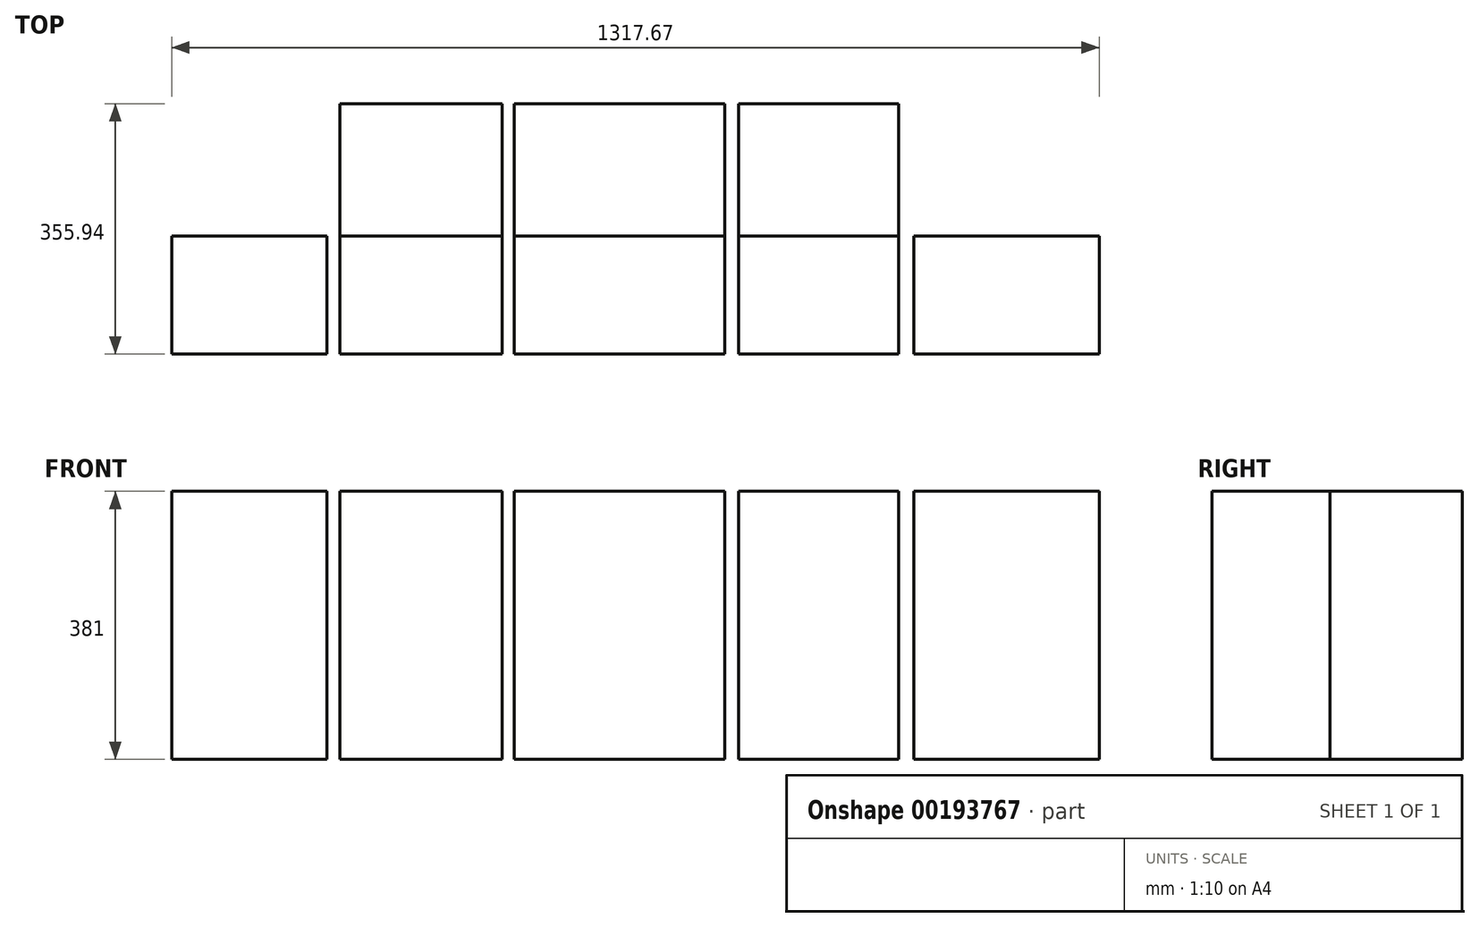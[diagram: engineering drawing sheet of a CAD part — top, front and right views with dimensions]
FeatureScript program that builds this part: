
annotation { "Feature Type Name" : "Feature", "Feature Type Description" : "" }
export const myFeature = defineFeature(function(context is Context, id is Id, definition is map)
    precondition{}
    {
        {
            var Q0;
            Q0=qCreatedBy(makeId("Top.planeOp"),FACE);
            var sketch = newSketch(context, id + "F0", { "sketchPlane" : qUnion([Q0])});
            skLineSegment(sketch, "E0.bottom", {"start": v(-149.74, -83.99) * mm, "end": v(149.74, -83.99) * mm});
            skLineSegment(sketch, "E0.top", {"start": v(-149.74, 83.99) * mm, "end": v(149.74, 83.99) * mm});
            skLineSegment(sketch, "E0.left", {"start": v(-149.74, -83.99) * mm, "end": v(-149.74, 83.99) * mm});
            skLineSegment(sketch, "E0.right", {"start": v(149.74, -83.99) * mm, "end": v(149.74, 83.99) * mm});
            skPoint(sketch, "E0.middle", {"position": v(0, 0) * mm});
            skLineSegment(sketch, "E1.bottom", {"start": v(-166.81, 83.99) * mm, "end": v(-397.4, 83.99) * mm});
            skLineSegment(sketch, "E1.top", {"start": v(-166.81, -83.99) * mm, "end": v(-397.4, -83.99) * mm});
            skLineSegment(sketch, "E1.left", {"start": v(-166.81, 83.99) * mm, "end": v(-166.81, -83.99) * mm});
            skLineSegment(sketch, "E1.right", {"start": v(-397.4, 83.99) * mm, "end": v(-397.4, -83.99) * mm});
            skLineSegment(sketch, "E2.bottom", {"start": v(-415.52, 83.99) * mm, "end": v(-636.23, 83.99) * mm});
            skLineSegment(sketch, "E2.top", {"start": v(-415.52, -83.99) * mm, "end": v(-636.23, -83.99) * mm});
            skLineSegment(sketch, "E2.left", {"start": v(-415.52, 83.99) * mm, "end": v(-415.52, -83.99) * mm});
            skLineSegment(sketch, "E2.right", {"start": v(-636.23, 83.99) * mm, "end": v(-636.23, -83.99) * mm});
            skLineSegment(sketch, "E3.bottom", {"start": v(169.2, 83.99) * mm, "end": v(396.5, 83.99) * mm});
            skLineSegment(sketch, "E3.top", {"start": v(169.2, -83.99) * mm, "end": v(396.5, -83.99) * mm});
            skLineSegment(sketch, "E3.left", {"start": v(169.2, 83.99) * mm, "end": v(169.2, -83.99) * mm});
            skLineSegment(sketch, "E3.right", {"start": v(396.5, 83.99) * mm, "end": v(396.5, -83.99) * mm});
            skLineSegment(sketch, "E4.bottom", {"start": v(417.9, 83.99) * mm, "end": v(681.44, 83.99) * mm});
            skLineSegment(sketch, "E4.top", {"start": v(417.9, -83.99) * mm, "end": v(681.44, -83.99) * mm});
            skLineSegment(sketch, "E4.left", {"start": v(417.9, 83.99) * mm, "end": v(417.9, -83.99) * mm});
            skLineSegment(sketch, "E4.right", {"start": v(681.44, 83.99) * mm, "end": v(681.44, -83.99) * mm});
            skSolve(sketch);
        }
        {
            var Q0;
            Q0=makeQuery(id+"F0.imprint","IMPRINT",FACE,{"disambiguationData":[TD([[makeQuery(id+"F0.imprint","IMPRINT",EDGE,{"derivedFrom":sQuery(id+"F0.wireOp",EDGE,"E2.bottom")}),1.0]])]});
            var Q1;
            Q1=makeQuery(id+"F0.imprint","IMPRINT",FACE,{"disambiguationData":[TD([[makeQuery(id+"F0.imprint","IMPRINT",EDGE,{"derivedFrom":sQuery(id+"F0.wireOp",EDGE,"E1.bottom")}),1.0]])]});
            var Q2;
            Q2=makeQuery(id+"F0.imprint","IMPRINT",FACE,{"disambiguationData":[TD([[makeQuery(id+"F0.imprint","IMPRINT",EDGE,{"derivedFrom":sQuery(id+"F0.wireOp",EDGE,"E0.bottom")}),1.0]])]});
            var Q3;
            Q3=makeQuery(id+"F0.imprint","IMPRINT",FACE,{"disambiguationData":[TD([[makeQuery(id+"F0.imprint","IMPRINT",EDGE,{"derivedFrom":sQuery(id+"F0.wireOp",EDGE,"E3.bottom")}),-1.0]])]});
            var Q4;
            Q4=makeQuery(id+"F0.imprint","IMPRINT",FACE,{"disambiguationData":[TD([[makeQuery(id+"F0.imprint","IMPRINT",EDGE,{"derivedFrom":sQuery(id+"F0.wireOp",EDGE,"E4.bottom")}),-1.0]])]});
            extrude(context, id + "F1", {"entities" : qUnion([Q0, Q1, Q2, Q3, Q4]), "depth" : 381 * mm});
        }
        {
            var Q0;
            Q0=makeQuery(id+"F1.opExtrude","SWEPT_FACE",FACE,{"disambiguationData":[OSD([sQuery(id+"F0.wireOp",EDGE,"E0.top")])]});
            var Q1;
            Q1=makeQuery(id+"F1.opExtrude","SWEPT_FACE",FACE,{"disambiguationData":[OSD([sQuery(id+"F0.wireOp",EDGE,"E1.bottom")])]});
            var Q2;
            Q2=makeQuery(id+"F1.opExtrude","SWEPT_FACE",FACE,{"disambiguationData":[OSD([sQuery(id+"F0.wireOp",EDGE,"E3.bottom")])]});
            extrude(context, id + "F2", {"entities" : qUnion([Q0, Q1, Q2]), "depth" : 187.96 * mm});
        }
    });
